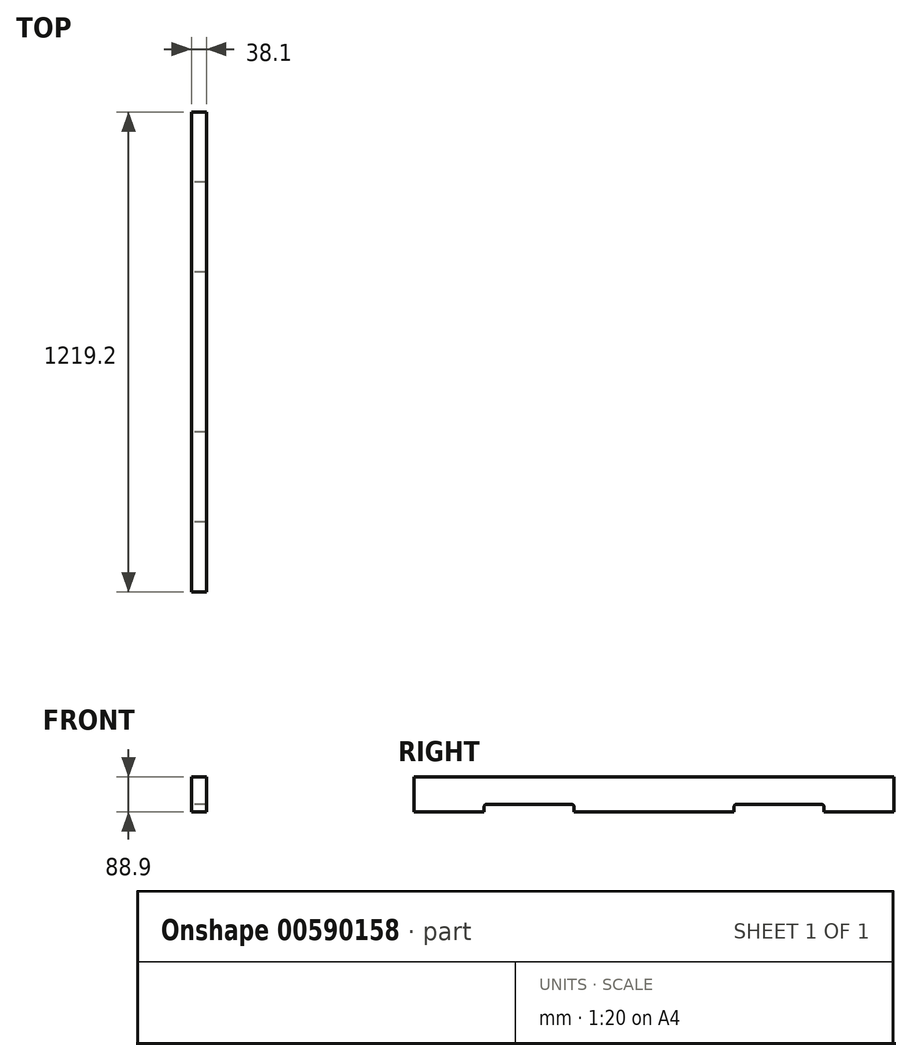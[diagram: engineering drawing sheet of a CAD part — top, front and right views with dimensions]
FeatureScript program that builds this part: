
annotation { "Feature Type Name" : "Feature", "Feature Type Description" : "" }
export const myFeature = defineFeature(function(context is Context, id is Id, definition is map)
    precondition{}
    {
        {
            var Q0;
            Q0=qCreatedBy(makeId("Front.planeOp"),FACE);
            var sketch = newSketch(context, id + "F0", { "sketchPlane" : qUnion([Q0])});
            skLineSegment(sketch, "E0.bottom", {"start": v(0, 0) * mm, "end": v(38.1, 0) * mm});
            skLineSegment(sketch, "E0.top", {"start": v(0, 88.9) * mm, "end": v(38.1, 88.9) * mm});
            skLineSegment(sketch, "E0.left", {"start": v(0, 0) * mm, "end": v(0, 88.9) * mm});
            skLineSegment(sketch, "E0.right", {"start": v(38.1, 0) * mm, "end": v(38.1, 88.9) * mm});
            skSolve(sketch);
        }
        {
            var Q0;
            Q0=qSketchRegion(id+"F0",true);
            extrude(context, id + "F1", {"entities" : qUnion([Q0]), "oppositeDirection" : true, "depth" : 1219.2 * mm, "offsetDistance" : 25.4 * mm});
        }
        {
            var Q0;
            Q0=makeQuery(id+"F1.opExtrude","SWEPT_FACE",FACE,{"disambiguationData":[OSD([sQuery(id+"F0.wireOp",EDGE,"E0.left")])]});
            var sketch = newSketch(context, id + "F2", { "sketchPlane" : qUnion([Q0])});
            skLineSegment(sketch, "E1", {"start": v(-1219.2, 0) * mm, "end": v(-1219.2, 221.82) * mm, "construction": true});
            skLineSegment(sketch, "E2", {"start": v(0, 0) * mm, "end": v(0, 206.56) * mm, "construction": true});
            skLineSegment(sketch, "E3.bottom", {"start": v(-1041.4, 0) * mm, "end": v(-812.8, 0) * mm});
            skLineSegment(sketch, "E3.top", {"start": v(-1035.05, 19.05) * mm, "end": v(-819.15, 19.05) * mm});
            skLineSegment(sketch, "E3.left", {"start": v(-1041.4, 0) * mm, "end": v(-1041.4, 12.7) * mm});
            skLineSegment(sketch, "E3.right", {"start": v(-812.8, 0) * mm, "end": v(-812.8, 12.7) * mm});
            skLineSegment(sketch, "E4.bottom", {"start": v(-406.4, 0) * mm, "end": v(-177.8, 0) * mm});
            skLineSegment(sketch, "E4.top", {"start": v(-400.05, 19.05) * mm, "end": v(-184.15, 19.05) * mm});
            skLineSegment(sketch, "E4.left", {"start": v(-406.4, 0) * mm, "end": v(-406.4, 12.7) * mm});
            skLineSegment(sketch, "E4.right", {"start": v(-177.8, 0) * mm, "end": v(-177.8, 12.7) * mm});
            skPoint(sketch, "E5.visualSharp", {"position": v(-1041.4, 19.05) * mm});
            skArc(sketch, "E5.filletArc", {"start": v(-1035.05, 19.05) * mm, "mid": v(-1039.54, 17.2) * mm, "end": v(-1041.4, 12.7) * mm});
            skPoint(sketch, "E6.visualSharp", {"position": v(-812.8, 19.05) * mm});
            skArc(sketch, "E6.filletArc", {"start": v(-812.8, 12.7) * mm, "mid": v(-814.66, 17.2) * mm, "end": v(-819.15, 19.05) * mm});
            skPoint(sketch, "E7.visualSharp", {"position": v(-406.4, 19.05) * mm});
            skArc(sketch, "E7.filletArc", {"start": v(-400.05, 19.05) * mm, "mid": v(-404.54, 17.2) * mm, "end": v(-406.4, 12.7) * mm});
            skPoint(sketch, "E8.visualSharp", {"position": v(-177.8, 19.05) * mm});
            skArc(sketch, "E8.filletArc", {"start": v(-177.8, 12.7) * mm, "mid": v(-179.66, 17.2) * mm, "end": v(-184.15, 19.05) * mm});
            skSolve(sketch);
        }
        {
            var Q0;
            Q0=qSketchRegion(id+"F2",true);
            extrude(context, id + "F3", {"entities" : qUnion([Q0]), "operationType" : NewBodyOperationType.REMOVE, "oppositeDirection" : true, "depth" : 1092.2 * mm, "offsetDistance" : 25.4 * mm});
        }
    });
